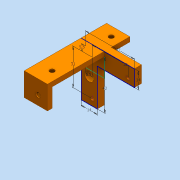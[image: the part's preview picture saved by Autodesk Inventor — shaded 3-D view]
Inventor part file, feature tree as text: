
AUTODESK INVENTOR PART (.ipt)
format: ipt  version: 2016 (Build 200138000, 138)  size: 229,888 bytes
history: native  units: mm
features: extrude x9, sketch x9, hole x7
ambient origin geometry x8: Origin, YZ Plane, XZ Plane, XY Plane, X Axis, Y Axis, Z Axis, Center Point
bodies: Solid1 (feature_tree)
feature tree (25):
  extrude  "Extrusion1"  Depth=20.0mm
  extrude  "Extrusion2"  Depth=45.0mm TaperAngle=0.0deg
  hole  "Hole2"  [1 undecoded]
  hole  "Hole3"  [1 undecoded]
  hole  "Hole4"  [1 undecoded]
  sketch  "Sketch3"  dims[d15=37.0mm d16=8.0mm d17=4.0mm d18=6.0mm d19=8.0mm d20=2.0mm d21=90.0deg d22=8.0mm d23=20.594885mm]
  sketch  "Sketch4"  dims[d24=37.0mm d25=8.0mm d26=4.0mm d27=6.0mm d28=8.0mm d29=2.0mm d30=90.0deg d31=8.0mm d32=20.594885mm]
  sketch  "Sketch5"  dims[d33=8.0mm d34=8.0mm d35=4.0mm d36=6.0mm d37=8.0mm d38=2.0mm d39=90.0deg d40=8.0mm d41=20.594885mm d51=7.0mm]
  extrude  "Extrusion3"  Depth=14.0mm
  extrude  "Extrusion4"  Depth=42.0mm
  extrude  "Extrusion5"  Depth=5.5mm
  sketch  "Sketch6"  dims[d52=7.0mm d53=7.0mm]
  extrude  "Extrusion6"  Depth=5.5mm
  hole  "Hole5"  [1 undecoded]
  extrude  "Extrusion7"  Depth=2.0mm
  hole  "Hole6"  [1 undecoded]
  hole  "Hole7"  [1 undecoded]
  sketch  "Sketch8"  dims[d58=3.2mm d59=0.0mm d62=14.0mm]
  extrude  "Extrusion8"  Depth=20.0mm
  extrude  "Extrusion9"  Depth=4.0mm
  hole  "Hole8"  [1 undecoded]
  sketch  "Sketch1"  dims[d0=20.0mm d1=20.0mm]
  sketch  "Sketch2"  dims[d2=4.0mm d3=0.0mm d4=45.0mm d5=0.0mm]
  sketch  "Sketch7"  dims[d54=3.2mm d55=0.0mm d56=3.2mm d57=0.0mm]
  sketch  "Sketch9"  dims[d65=42.0mm d66=42.0mm d68=5.5mm d69=5.5mm d70=31.0mm d71=31.0mm d72=14.0mm d73=6.0mm d74=0.0mm d75=3.0mm d76=6.0mm d77=4.0mm d78=2.0mm d79=90.0deg d80=8.0mm d81=20.594885mm d82=20.0mm d83=4.0mm d84=4.0mm d85=20.0mm d86=16.0mm d87=0.0mm d88=8.0mm d89=8.0mm d90=4.0mm d91=6.0mm d92=4.0mm d93=2.0mm d94=90.0deg d95=8.0mm d96=20.594885mm d97=8.0mm d98=8.0mm d99=4.0mm d100=6.0mm d101=4.0mm d102=2.0mm d103=90.0deg d104=8.0mm d105=20.594885mm d106=7.0mm d107=7.0mm d108=3.2mm d109=0.0mm d110=3.2mm d111=0.0mm d112=7.0mm d113=21.0mm d114=8.0mm d115=6.0mm d116=4.0mm d117=2.0mm d118=90.0deg d119=8.0mm d120=20.594885mm]
note: 7 required parameter values undecoded (feature->parameter linkage not recoverable at this tier; creation-order binding heuristic only, values carry confidence <= 0.55)
